# Revit family: SU-6000_GENERADO
name_source: partatom
category: Equipos especializados
units: mm (PartAtom-declared; Revit-internal decimal feet)

## family parameters
Compartido = No
Corte con vacíos al cargar = No
Cota de conector redondo = Diámetro de uso
Número OmniClass = 23.21.21.47
Punto de cálculo de habitación = No
Se basa en plano de trabajo = No
Siempre vertical = Sí
Tipo de pieza = Normal

## types (11) — shared parameters
Depth = 874 mm  [stored 2.86745 ft]
Fabricante = SAMMIC S.L.
Foodservice Equipment Identifier = Sí
Height = 1370 mm  [stored 4.49475 ft]
Phase = 3
Revision Code = 1
URL = https://www.sammic.com
URL Cutsheet = http://www.sammic.com
Width = 1640 mm  [stored 5.38058 ft]
zero-valued in all types: Elevación por defecto

## per-type parameters (varying)
| type | Comentarios de tipo | Conn Plug | Cycle | Electric Connection Type | FL Amps | HP | Modelo | Specification by Manufacturer | Volts | Watts | Weight in Pounds |
| Vacuum packing machine SU-6100 400/50-60/3N | Double chamber vacuum packing machine. 100m³/h. |  | 50 Hz | 3P+N+G | 9 A | 5.36 | 1141030 | High performance model with tilting cover, double chamber and 4 x 662 mm. sealing bars.
100 m­³/h Busch vacuum pump.
Vacuum controlled by sensor. | 400 V | 4000 W | 793.7 |
| Vacuum packing machine SU-6100P 400/50-60/3N | Double chamber vacuum packing machine. 100m³/h. |  | 50 Hz | 3P+N+G | 9 A | 5.36 | 1141033 | High performance model with tilting cover, double chamber and 4 x 662 mm. sealing bars.
100 m­³/h Busch vacuum pump.
Vacuum controlled by sensor. | 400 V | 4000 W | 793.7 |
| Vacuum packing machine SU-6100P+ 400/50-60/3N | Double chamber vacuum packing machine. 100m³/h. |  | 50 Hz | 3P+N+G | 9 A | 5.36 | 1141035 | High performance model with tilting cover, double chamber and 4 x 662 mm. sealing bars.
100 m­³/h Busch vacuum pump.
Vacuum controlled by sensor. | 400 V | 4000 W | 793.7 |
| Vacuum packing machine SU-6100P 220/60/3 | Double chamber vacuum packing machine. 100m³/h. |  | 60 Hz | 3P+N+G | 15 A | 6.97 | 1141043 | High performance model with tilting cover, double chamber and 4 x 662 mm. sealing bars.
100 m­³/h Busch vacuum pump.
Vacuum controlled by sensor. | 220 V | 5200 W | 793.7 |
| Vacuum packing machine SU-6100P+ 220/60/3 | Double chamber vacuum packing machine. 100m³/h. |  | 60 Hz | 3P+N+G | 15 A | 6.97 | 1141045 | High performance model with tilting cover, double chamber and 4 x 662 mm. sealing bars.
100 m­³/h Busch vacuum pump.
Vacuum controlled by sensor. | 220 V | 5200 W | 793.7 |
| Vacuum packing machine SU-6100P 208-240/60/3 USA | Double chamber vacuum packing machine. 100m³/h.

ELECTRICAL DATA:

240V/60Hz/3~ (16A) | USA (NEMA L15-30P / 3P+G) | 60 Hz |  | 16 A |  | 1141069 | High performance model with tilting cover, double chamber and 4 x 662 mm. sealing bars.
100 m­³/h Busch vacuum pump.
Vacuum controlled by sensor. | 208 V | 0 W | 793.7 |
| Vacuum packing machine SU-6160P 400/50-60/3N | Double chamber vacuum packing machine. 155 m­³/h. |  | 50 Hz | 3P+N+G | 12 A | 8.05 | 1141053 | High performance model with tilting cover, double chamber and 4 x 662 mm. sealing bars.
155 m­³/h. Busch vacuum pump.
Vacuum controlled by sensor. | 400 V | 6000 W | 881.8 |
| Vacuum packing machine SU-6160P+ 400/50-60/3N | Double chamber vacuum packing machine. 155 m­³/h. |  | 50 Hz | 3P+N+G | 12 A | 8.05 | 1141055 | High performance model with tilting cover, double chamber and 4 x 662 mm. sealing bars.
155 m­³/h. Busch vacuum pump.
Vacuum controlled by sensor. | 400 V | 6000 W | 881.8 |
| Vacuum packing machine SU-6160P 220/60/3 | Double chamber vacuum packing machine. 155 m­³/h. |  | 60 Hz | 3P+N+G | 17 A | 8.05 | 1141063 | High performance model with tilting cover, double chamber and 4 x 662 mm. sealing bars.
155 m­³/h. Busch vacuum pump.
Vacuum controlled by sensor. | 220 V | 6000 W | 881.8 |
| Vacuum packing machine SU-6160P+ 220/60/3 | Double chamber vacuum packing machine. 155 m­³/h. |  | 60 Hz | 3P+N+G | 17 A | 8.05 | 1141065 | High performance model with tilting cover, double chamber and 4 x 662 mm. sealing bars.
155 m­³/h. Busch vacuum pump.
Vacuum controlled by sensor. | 220 V | 6000 W | 881.8 |
| Vacuum packing machine SU-6160P 208-240/60/3 USA | Double chamber vacuum packing machine. 155 m­³/h.

ELECTRICAL DATA:

240V/60Hz/3~ (16A) | USA (NEMA L15-30P / 3P+G) | 60 Hz |  | 16 A |  | 1141070 | High performance model with tilting cover, double chamber and 4 x 662 mm. sealing bars.
155 m­³/h. Busch vacuum pump.
Vacuum controlled by sensor. | 208 V | 0 W | 881.8 |

note: column(s) folded — value = type name in every type: Descripción

note: [stored X ft] marks values corroborated as IEEE doubles in the binary element streams (Revit-internal decimal feet)
